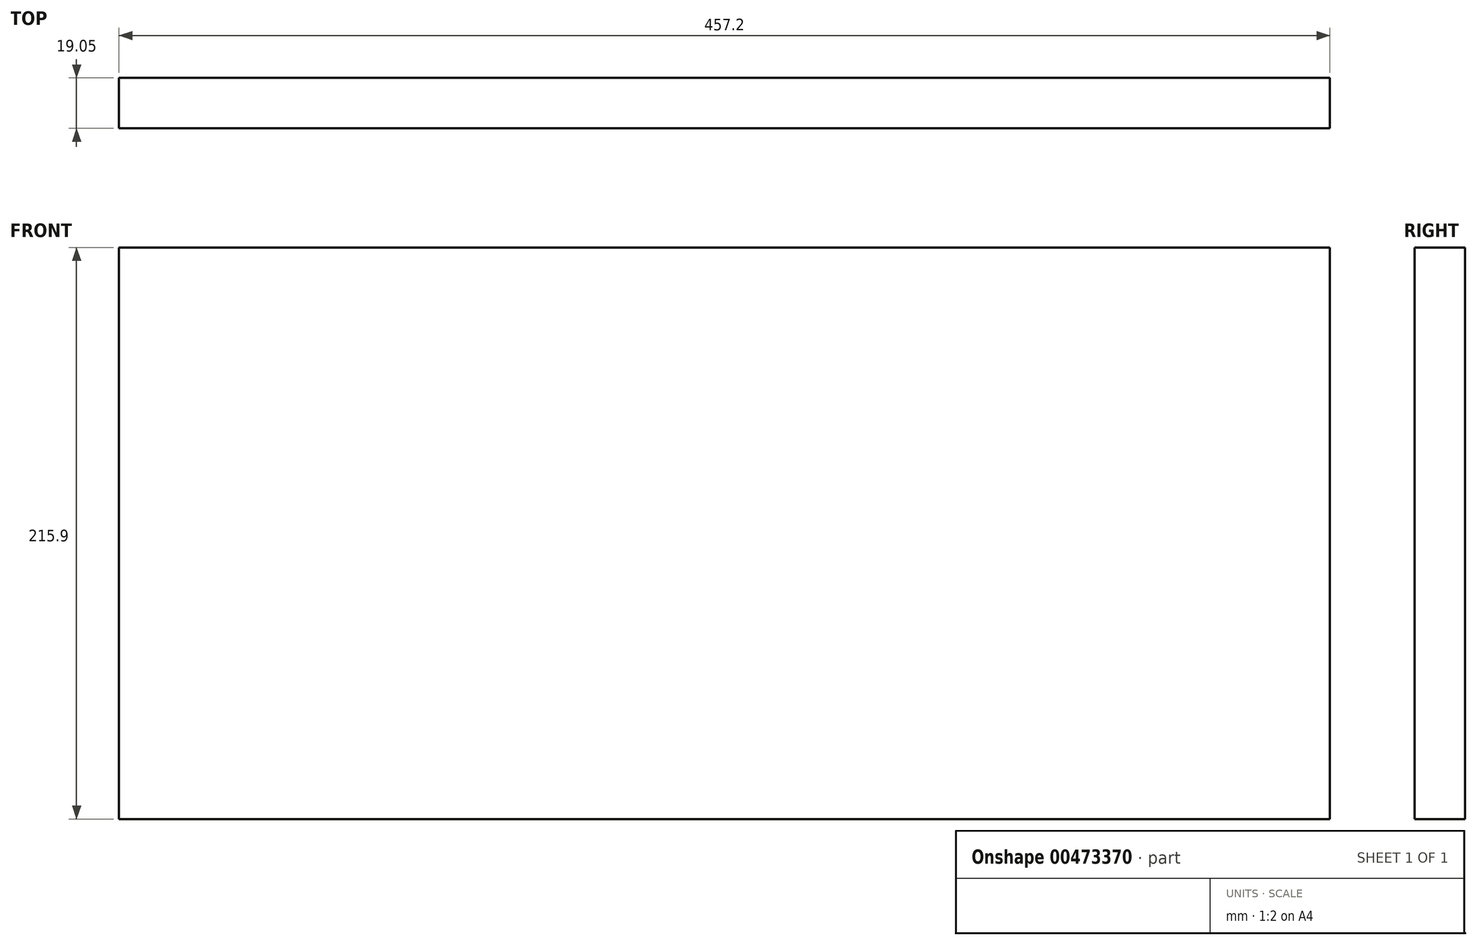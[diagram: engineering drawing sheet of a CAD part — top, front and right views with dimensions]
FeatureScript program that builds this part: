
annotation { "Feature Type Name" : "Feature", "Feature Type Description" : "" }
export const myFeature = defineFeature(function(context is Context, id is Id, definition is map)
    precondition{}
    {
        {
            var Q0;
            Q0=qCreatedBy(makeId("Front.planeOp"),FACE);
            var sketch = newSketch(context, id + "F0", { "sketchPlane" : qUnion([Q0])});
            skLineSegment(sketch, "E0.bottom", {"start": v(-218.85, 15.24) * mm, "end": v(238.35, 15.24) * mm});
            skLineSegment(sketch, "E0.top", {"start": v(-218.85, -200.66) * mm, "end": v(238.35, -200.66) * mm});
            skLineSegment(sketch, "E0.left", {"start": v(-218.85, 15.24) * mm, "end": v(-218.85, -200.66) * mm});
            skLineSegment(sketch, "E0.right", {"start": v(238.35, 15.24) * mm, "end": v(238.35, -200.66) * mm});
            skSolve(sketch);
        }
        {
            var Q0;
            Q0=makeQuery(id+"F0.imprint","IMPRINT",FACE,{"disambiguationData":[TD([[makeQuery(id+"F0.imprint","IMPRINT",EDGE,{"derivedFrom":sQuery(id+"F0.wireOp",EDGE,"E0.bottom")}),-1.0]])]});
            extrude(context, id + "F2", {"entities" : qUnion([Q0]), "depth" : 19.05 * mm});
        }
    });
